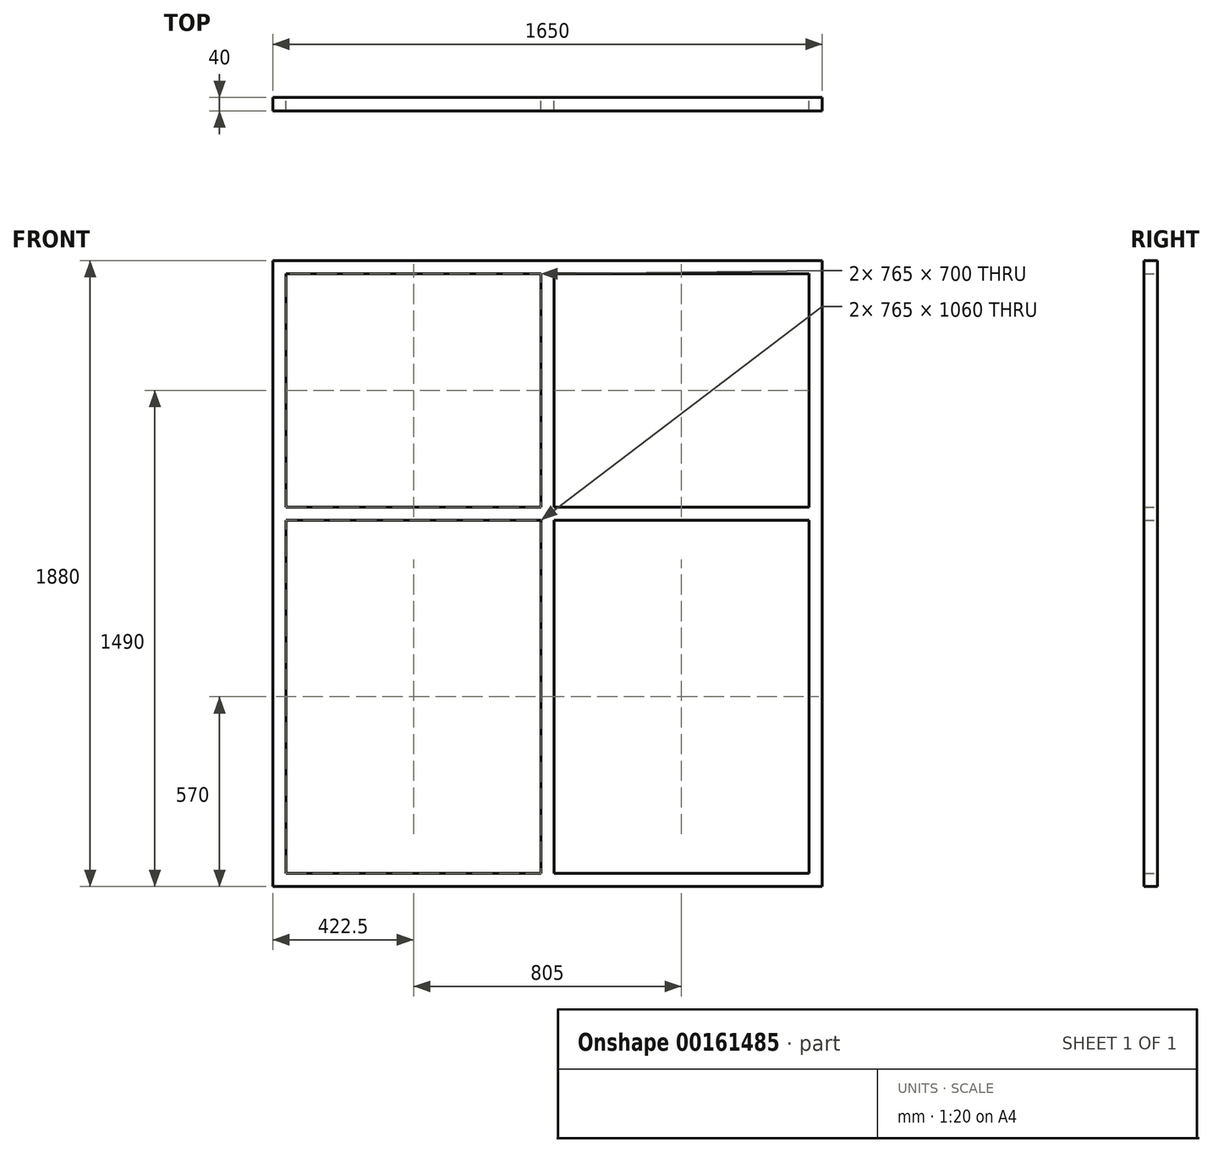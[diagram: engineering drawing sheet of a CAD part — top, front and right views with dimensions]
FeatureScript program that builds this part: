
annotation { "Feature Type Name" : "Feature", "Feature Type Description" : "" }
export const myFeature = defineFeature(function(context is Context, id is Id, definition is map)
    precondition{}
    {
        {
            var Q0;
            Q0=qCreatedBy(makeId("Front.planeOp"),FACE);
            var sketch = newSketch(context, id + "F0", { "sketchPlane" : qUnion([Q0])});
            skLineSegment(sketch, "E0.bottom", {"start": v(-825, 940) * mm, "end": v(825, 940) * mm});
            skLineSegment(sketch, "E0.top", {"start": v(-825, -940) * mm, "end": v(825, -940) * mm});
            skLineSegment(sketch, "E0.left", {"start": v(-825, 940) * mm, "end": v(-825, -940) * mm});
            skLineSegment(sketch, "E0.right", {"start": v(825, 940) * mm, "end": v(825, -940) * mm});
            skPoint(sketch, "E0.middle", {"position": v(0, 0) * mm});
            skLineSegment(sketch, "E1.bottom", {"start": v(-785, 900) * mm, "end": v(-20, 900) * mm});
            skLineSegment(sketch, "E1.top", {"start": v(-785, -900) * mm, "end": v(-20, -900) * mm});
            skLineSegment(sketch, "E1.left", {"start": v(-785, 900) * mm, "end": v(-785, 200) * mm});
            skLineSegment(sketch, "E1.right", {"start": v(785, 900) * mm, "end": v(785, 200) * mm});
            skLineSegment(sketch, "E2.left", {"start": v(-20, 900) * mm, "end": v(-20, 200) * mm});
            skLineSegment(sketch, "E2.right", {"start": v(20, 900) * mm, "end": v(20, 200) * mm});
            skLineSegment(sketch, "E3.trimOffspring", {"start": v(20, 900) * mm, "end": v(785, 900) * mm});
            skLineSegment(sketch, "E4.trimOffspring", {"start": v(20, -900) * mm, "end": v(785, -900) * mm});
            skLineSegment(sketch, "E5.bottom", {"start": v(-785, 200) * mm, "end": v(-20, 200) * mm});
            skLineSegment(sketch, "E5.top", {"start": v(-785, 160) * mm, "end": v(-20, 160) * mm});
            skLineSegment(sketch, "E6.trimOffspring", {"start": v(20, 200) * mm, "end": v(785, 200) * mm});
            skLineSegment(sketch, "E7.trimOffspring", {"start": v(20, 160) * mm, "end": v(785, 160) * mm});
            skLineSegment(sketch, "E8.trimOffspring", {"start": v(-20, 160) * mm, "end": v(-20, -900) * mm});
            skLineSegment(sketch, "E9.trimOffspring", {"start": v(20, 160) * mm, "end": v(20, -900) * mm});
            skLineSegment(sketch, "E10.trimOffspring", {"start": v(785, 160) * mm, "end": v(785, -900) * mm});
            skLineSegment(sketch, "E11.trimOffspring", {"start": v(-785, 160) * mm, "end": v(-785, -900) * mm});
            skSolve(sketch);
        }
        {
            var Q0;
            Q0 = qSketchRegion(id + "F0", true);
            extrude(context, id + "F1", {"entities" : qUnion([Q0]), "endBound" : BoundingType.SYMMETRIC, "depth" : 40 * mm, "offsetDistance" : 25 * mm});
        }
    });
